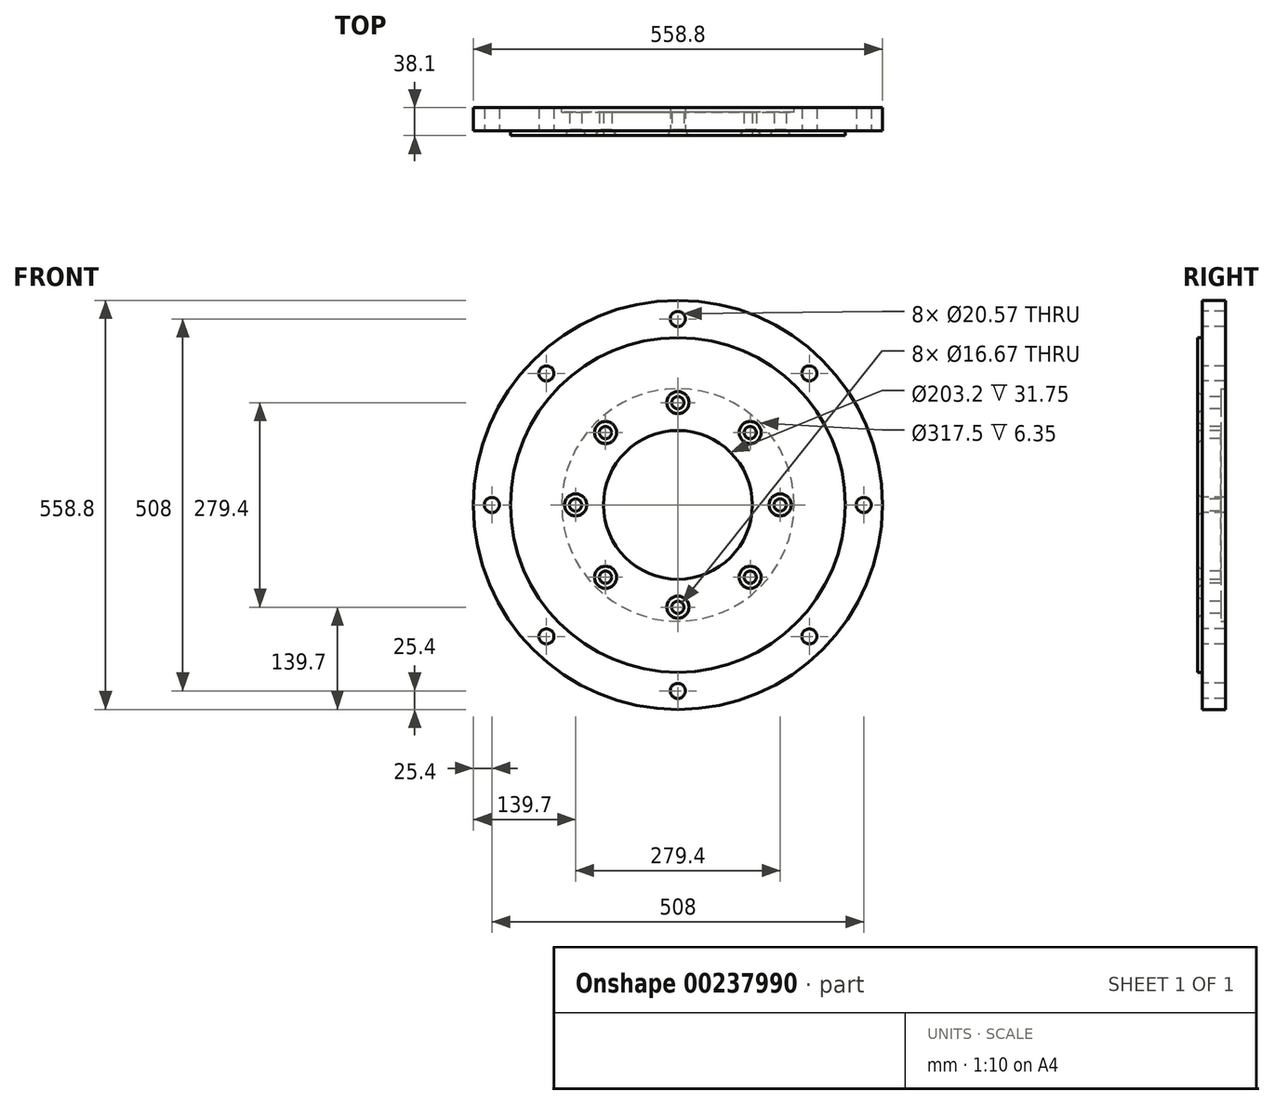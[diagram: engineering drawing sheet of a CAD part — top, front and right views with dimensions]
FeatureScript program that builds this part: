
annotation { "Feature Type Name" : "Feature", "Feature Type Description" : "" }
export const myFeature = defineFeature(function(context is Context, id is Id, definition is map)
    precondition{}
    {
        {
            var Q0;
            Q0=qCreatedBy(makeId("Front.planeOp"),FACE);
            var sketch = newSketch(context, id + "F0", { "sketchPlane" : qUnion([Q0])});
            skCircle(sketch, "E0", {"center": v(0, 0) * mm, "radius": 279.4 * mm});
            skSolve(sketch);
        }
        {
            var Q0;
            Q0=makeQuery(id+"F0.imprint","IMPRINT",FACE,{"disambiguationData":[TD([[makeQuery(id+"F0.imprint","IMPRINT",EDGE,{"derivedFrom":sQuery(id+"F0.wireOp",EDGE,"E0")}),1.0]])]});
            extrude(context, id + "F1", {"entities" : qUnion([Q0]), "depth" : 38.1 * mm});
        }
        {
            var Q0;
            Q0=makeQuery(id+"F1.opExtrude","CAP_FACE",FACE,{"disambiguationData":[OSD([sQuery(id+"F0.wireOp",EDGE,"E0")])],"isStart":false});
            var sketch = newSketch(context, id + "F2", { "sketchPlane" : qUnion([Q0])});
            skCircle(sketch, "E1", {"center": v(0, 0) * mm, "radius": 228.6 * mm});
            skSolve(sketch);
        }
        {
            var Q0;
            Q0=makeQuery(id+"F2.imprint","IMPRINT",FACE,{"disambiguationData":[TD([[makeQuery(id+"F2.imprint","IMPRINT",EDGE,{"derivedFrom":sQuery(id+"F2.wireOp",EDGE,"E1")}),-1.0]])]});
            extrude(context, id + "F3", {"entities" : qUnion([Q0]), "operationType" : NewBodyOperationType.REMOVE, "oppositeDirection" : true, "depth" : 6.35 * mm});
        }
        {
            var Q0;
            Q0=makeQuery(id+"F3.boolean.opBoolean","COPY",FACE,{"derivedFrom":makeQuery(id+"F3.opExtrude","CAP_FACE",FACE,{"disambiguationData":[OSD([sQuery(id+"F0.wireOp",EDGE,"E0"),sQuery(id+"F2.wireOp",EDGE,"E1")])],"isStart":false})});
            var sketch = newSketch(context, id + "F4", { "sketchPlane" : qUnion([Q0])});
            skPoint(sketch, "E2", {"position": v(254, 0) * mm});
            skPoint(sketch, "E3.1.0", {"position": v(179.6, 179.6) * mm});
            skPoint(sketch, "E3.2.0", {"position": v(0, 254) * mm});
            skPoint(sketch, "E3.3.0", {"position": v(-179.6, 179.6) * mm});
            skPoint(sketch, "E3.4.0", {"position": v(-254, 0) * mm});
            skPoint(sketch, "E3.5.0", {"position": v(-179.6, -179.6) * mm});
            skPoint(sketch, "E3.6.0", {"position": v(0, -254) * mm});
            skPoint(sketch, "E3.7.0", {"position": v(179.6, -179.6) * mm});
            skPoint(sketch, "E3.center", {"position": v(0, 0) * mm});
            skSolve(sketch);
        }
        {
            var Q0;
            Q0=sQuery(id+"F4.wireOp",VERTEX,"E3.1.0");
            var Q1;
            Q1=sQuery(id+"F4.wireOp",VERTEX,"E2");
            var Q2;
            Q2=sQuery(id+"F4.wireOp",VERTEX,"E3.7.0");
            var Q3;
            Q3=sQuery(id+"F4.wireOp",VERTEX,"E3.6.0");
            var Q4;
            Q4=sQuery(id+"F4.wireOp",VERTEX,"E3.5.0");
            var Q5;
            Q5=sQuery(id+"F4.wireOp",VERTEX,"E3.2.0");
            var Q6;
            Q6=sQuery(id+"F4.wireOp",VERTEX,"E3.3.0");
            var Q7;
            Q7=sQuery(id+"F4.wireOp",VERTEX,"E3.4.0");
            var Q8;
            Q8=makeQuery(id+"F1.opExtrude","SWEPT_BODY",BODY,{"disambiguationData":[OSD([sQuery(id+"F0.wireOp",EDGE,"E0")])]});
            hole(context, id + "F5", {"style" : HoleStyle.SIMPLE, "endStyle" : HoleEndStyle.THROUGH, "holeDiameter" : 20.57 * mm, "locations" : qUnion([Q0, Q1, Q2, Q3, Q4, Q5, Q6, Q7]), "scope" : qUnion([Q8]), "isTappedThrough" : true});
        }
        {
            var Q0;
            Q0=makeQuery(id+"F1.opExtrude","CAP_FACE",FACE,{"disambiguationData":[OSD([sQuery(id+"F0.wireOp",EDGE,"E0")])],"isStart":false});
            var sketch = newSketch(context, id + "F6", { "sketchPlane" : qUnion([Q0])});
            skCircle(sketch, "E4", {"center": v(0, 0) * mm, "radius": 101.6 * mm});
            skSolve(sketch);
        }
        {
            var Q0;
            Q0=makeQuery(id+"F6.imprint","IMPRINT",FACE,{"disambiguationData":[TD([[makeQuery(id+"F6.imprint","IMPRINT",EDGE,{"derivedFrom":sQuery(id+"F6.wireOp",EDGE,"E4")}),1.0]])]});
            extrude(context, id + "F7", {"entities" : qUnion([Q0]), "operationType" : NewBodyOperationType.REMOVE, "endBound" : BoundingType.THROUGH_ALL, "oppositeDirection" : true, "depth" : 25.4 * mm});
        }
        {
            var Q0;
            Q0=makeQuery(id+"F1.opExtrude","CAP_FACE",FACE,{"disambiguationData":[OSD([sQuery(id+"F0.wireOp",EDGE,"E0")])],"isStart":true});
            var sketch = newSketch(context, id + "F8", { "sketchPlane" : qUnion([Q0])});
            skCircle(sketch, "E5", {"center": v(0, 0) * mm, "radius": 158.75 * mm});
            skSolve(sketch);
        }
        {
            var Q0;
            Q0=makeQuery(id+"F8.imprint","IMPRINT",FACE,{"disambiguationData":[TD([[makeQuery(id+"F8.imprint","IMPRINT",EDGE,{"derivedFrom":sQuery(id+"F8.wireOp",EDGE,"E5")}),1.0]])]});
            extrude(context, id + "F9", {"entities" : qUnion([Q0]), "operationType" : NewBodyOperationType.REMOVE, "oppositeDirection" : true, "depth" : 6.35 * mm});
        }
        {
            var Q0;
            Q0=makeQuery(id+"F1.opExtrude","CAP_FACE",FACE,{"disambiguationData":[OSD([sQuery(id+"F0.wireOp",EDGE,"E0")])],"isStart":false});
            var sketch = newSketch(context, id + "F10", { "sketchPlane" : qUnion([Q0])});
            skPoint(sketch, "E6", {"position": v(139.7, 0) * mm});
            skPoint(sketch, "E7.1.0", {"position": v(98.78, 98.78) * mm});
            skPoint(sketch, "E7.2.0", {"position": v(0, 139.7) * mm});
            skPoint(sketch, "E7.3.0", {"position": v(-98.78, 98.78) * mm});
            skPoint(sketch, "E7.4.0", {"position": v(-139.7, 0) * mm});
            skPoint(sketch, "E7.5.0", {"position": v(-98.78, -98.78) * mm});
            skPoint(sketch, "E7.6.0", {"position": v(0, -139.7) * mm});
            skPoint(sketch, "E7.7.0", {"position": v(98.78, -98.78) * mm});
            skPoint(sketch, "E7.center", {"position": v(0, 0) * mm});
            skSolve(sketch);
        }
        {
            var Q0;
            Q0=sQuery(id+"F10.wireOp",VERTEX,"E6");
            var Q1;
            Q1=sQuery(id+"F10.wireOp",VERTEX,"E7.1.0");
            var Q2;
            Q2=sQuery(id+"F10.wireOp",VERTEX,"E7.2.0");
            var Q3;
            Q3=sQuery(id+"F10.wireOp",VERTEX,"E7.3.0");
            var Q4;
            Q4=sQuery(id+"F10.wireOp",VERTEX,"E7.4.0");
            var Q5;
            Q5=sQuery(id+"F10.wireOp",VERTEX,"E7.5.0");
            var Q6;
            Q6=sQuery(id+"F10.wireOp",VERTEX,"E7.6.0");
            var Q7;
            Q7=sQuery(id+"F10.wireOp",VERTEX,"E7.7.0");
            var Q8;
            Q8=makeQuery(id+"F1.opExtrude","SWEPT_BODY",BODY,{"disambiguationData":[OSD([sQuery(id+"F0.wireOp",EDGE,"E0")])]});
            hole(context, id + "F11", {"style" : HoleStyle.C_SINK, "endStyle" : HoleEndStyle.THROUGH, "standardTappedOrClearance" : lookupTablePath({ "standard" : "ANSI", "fit" : "Normal (ASME)", "size" : "5/8", "type" : "Clearance" }), "standardBlindInLast" : lookupTablePath({ "fit" : "Free", "standard" : "ANSI", "size" : "5/8", "type" : "Clearance" }), "holeDiameter" : 16.67 * mm, "cSinkDiameter" : 30.18 * mm, "cSinkAngle" : 82 * degree, "locations" : qUnion([Q0, Q1, Q2, Q3, Q4, Q5, Q6, Q7]), "scope" : qUnion([Q8]), "isTappedThrough" : true});
        }
    });
